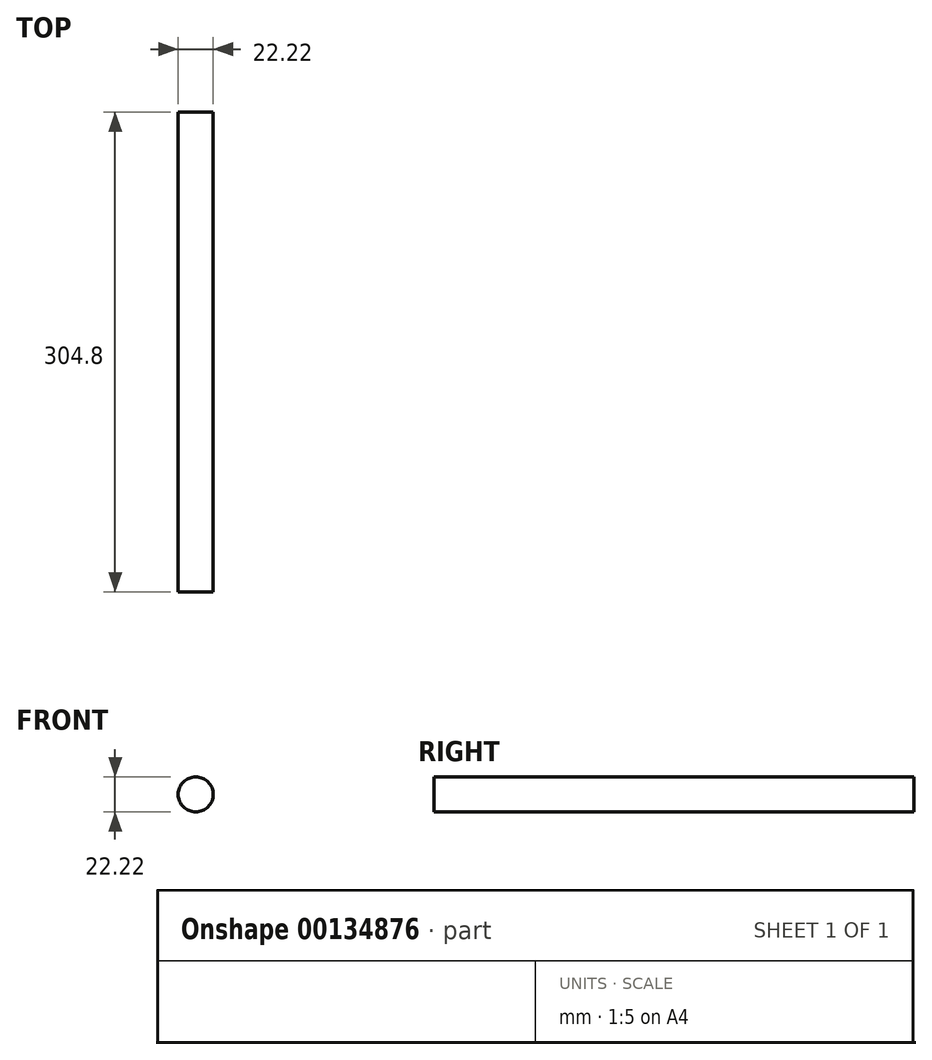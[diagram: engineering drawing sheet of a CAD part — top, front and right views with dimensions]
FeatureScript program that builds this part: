
annotation { "Feature Type Name" : "Feature", "Feature Type Description" : "" }
export const myFeature = defineFeature(function(context is Context, id is Id, definition is map)
    precondition{}
    {
        {
            var Q0;
            Q0=qCreatedBy(makeId("Front.planeOp"),FACE);
            var sketch = newSketch(context, id + "F0", { "sketchPlane" : qUnion([Q0])});
            skCircle(sketch, "E0", {"center": v(0, 0) * mm, "radius": 11.11 * mm});
            skSolve(sketch);
        }
        {
            var Q0;
            Q0 = qSketchRegion(id + "F0", true);
            extrude(context, id + "F1", {"entities" : qUnion([Q0]), "depth" : 304.8 * mm, "symmetric" : true});
        }
    });
